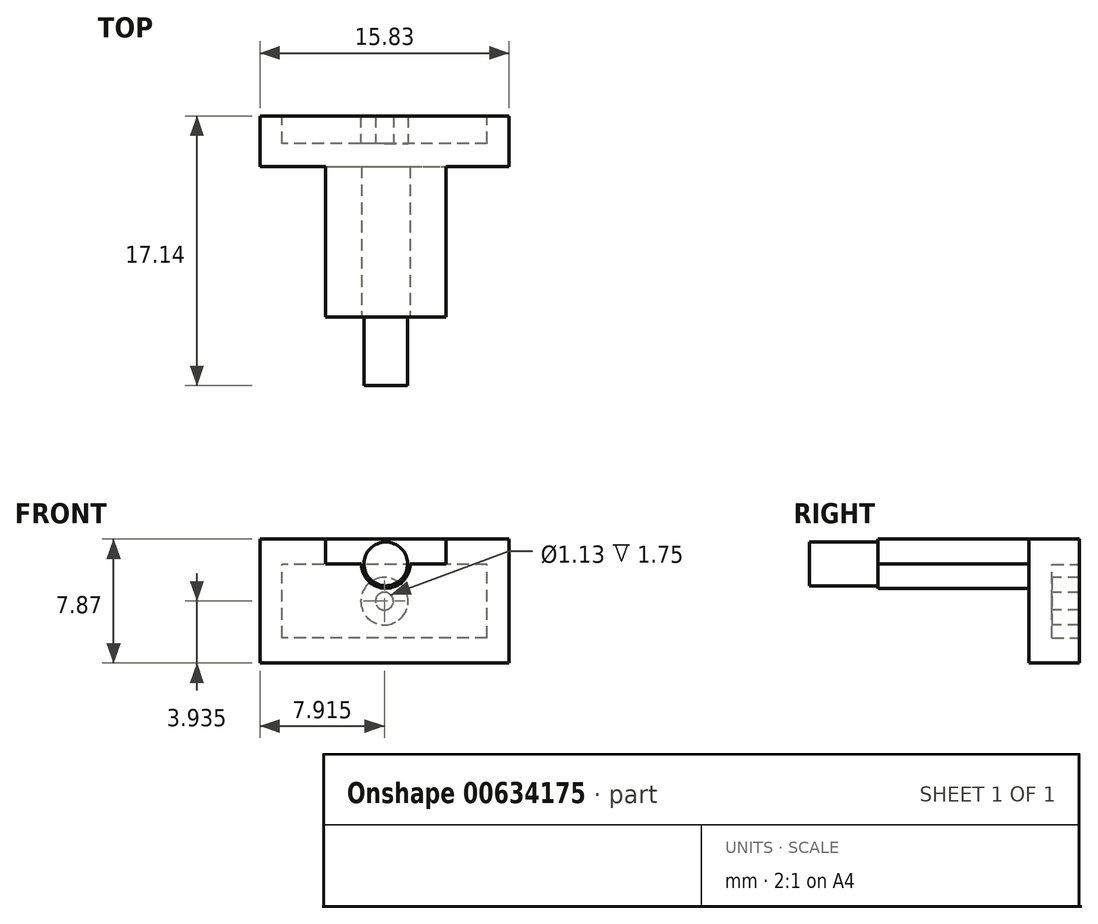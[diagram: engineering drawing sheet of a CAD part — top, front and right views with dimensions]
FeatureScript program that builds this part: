
annotation { "Feature Type Name" : "Feature", "Feature Type Description" : "" }
export const myFeature = defineFeature(function(context is Context, id is Id, definition is map)
    precondition{}
    {
        {
            var Q0;
            Q0=qCreatedBy(makeId("Front.planeOp"),FACE);
            var sketch = newSketch(context, id + "F0", { "sketchPlane" : qUnion([Q0])});
            skLineSegment(sketch, "E0.bottom", {"start": v(0, 0) * mm, "end": v(15.83, 0) * mm});
            skLineSegment(sketch, "E0.top", {"start": v(0, 7.87) * mm, "end": v(15.83, 7.87) * mm});
            skLineSegment(sketch, "E0.left", {"start": v(0, 0) * mm, "end": v(0, 7.87) * mm});
            skLineSegment(sketch, "E0.right", {"start": v(15.83, 0) * mm, "end": v(15.83, 7.87) * mm});
            skSolve(sketch);
        }
        {
            var Q0;
            Q0=qSketchRegion(id+"F0",true);
            extrude(context, id + "F1", {"entities" : qUnion([Q0]), "depth" : 3.2 * mm});
        }
        {
            var Q0;
            Q0=makeQuery(id+"F1.opExtrude","CAP_FACE",FACE,{"disambiguationData":[OSD([sQuery(id+"F0.wireOp",EDGE,"E0.bottom"),sQuery(id+"F0.wireOp",EDGE,"E0.top"),sQuery(id+"F0.wireOp",EDGE,"E0.left"),sQuery(id+"F0.wireOp",EDGE,"E0.right")])],"isStart":true});
            var sketch = newSketch(context, id + "F2", { "sketchPlane" : qUnion([Q0])});
            skLineSegment(sketch, "E1.bottom", {"start": v(-14.43, 1.6) * mm, "end": v(-1.4, 1.6) * mm});
            skLineSegment(sketch, "E1.top", {"start": v(-14.43, 6.27) * mm, "end": v(-1.4, 6.27) * mm});
            skLineSegment(sketch, "E1.left", {"start": v(-14.43, 1.6) * mm, "end": v(-14.43, 6.27) * mm});
            skLineSegment(sketch, "E1.right", {"start": v(-1.4, 1.6) * mm, "end": v(-1.4, 6.27) * mm});
            skSolve(sketch);
        }
        {
            var Q0;
            Q0=qSketchRegion(id+"F2",true);
            extrude(context, id + "F3", {"entities" : qUnion([Q0]), "operationType" : NewBodyOperationType.REMOVE, "oppositeDirection" : true, "depth" : 1.75 * mm});
        }
        {
            var Q0;
            Q0=makeQuery(id+"F3.boolean.opBoolean","COPY",FACE,{"derivedFrom":makeQuery(id+"F3.opExtrude","CAP_FACE",FACE,{"disambiguationData":[OSD([sQuery(id+"F2.wireOp",EDGE,"E1.bottom"),sQuery(id+"F2.wireOp",EDGE,"E1.top"),sQuery(id+"F2.wireOp",EDGE,"E1.left"),sQuery(id+"F2.wireOp",EDGE,"E1.right")])],"isStart":false})});
            var sketch = newSketch(context, id + "F4", { "sketchPlane" : qUnion([Q0])});
            skCircle(sketch, "E2", {"center": v(-7.92, 3.93) * mm, "radius": 1.5 * mm});
            skPoint(sketch, "E2.centerSnap0", {"position": v(-1.4, 3.93) * mm});
            skPoint(sketch, "E2.centerSnap1", {"position": v(-7.92, 6.27) * mm});
            skCircle(sketch, "E3", {"center": v(-7.92, 3.93) * mm, "radius": 0.56 * mm});
            skSolve(sketch);
        }
        {
            var Q0;
            Q0=qSketchRegion(id+"F4",true);
            var Q1;
            Q1=makeQuery(id+"F1.opExtrude","CAP_FACE",FACE,{"disambiguationData":[OSD([sQuery(id+"F0.wireOp",EDGE,"E0.bottom"),sQuery(id+"F0.wireOp",EDGE,"E0.top"),sQuery(id+"F0.wireOp",EDGE,"E0.left"),sQuery(id+"F0.wireOp",EDGE,"E0.right")])],"isStart":true});
            extrude(context, id + "F5", {"entities" : qUnion([Q0]), "operationType" : NewBodyOperationType.ADD, "endBound" : BoundingType.UP_TO_SURFACE, "endBoundEntityFace" : qUnion([Q1]), "depth" : 2 * mm});
        }
        {
            var Q0;
            Q0=makeQuery(id+"F1.opExtrude","CAP_FACE",FACE,{"disambiguationData":[OSD([sQuery(id+"F0.wireOp",EDGE,"E0.bottom"),sQuery(id+"F0.wireOp",EDGE,"E0.top"),sQuery(id+"F0.wireOp",EDGE,"E0.left"),sQuery(id+"F0.wireOp",EDGE,"E0.right")])],"isStart":false});
            var sketch = newSketch(context, id + "F6", { "sketchPlane" : qUnion([Q0])});
            skLineSegment(sketch, "E4.bottom", {"start": v(4.17, 7.87) * mm, "end": v(11.83, 7.87) * mm});
            skLineSegment(sketch, "E4.top", {"start": v(4.17, 6.3) * mm, "end": v(11.83, 6.3) * mm});
            skLineSegment(sketch, "E4.left", {"start": v(4.17, 7.87) * mm, "end": v(4.17, 6.3) * mm});
            skLineSegment(sketch, "E4.right", {"start": v(11.83, 7.87) * mm, "end": v(11.83, 6.3) * mm});
            skSolve(sketch);
        }
        {
            var Q0;
            Q0=qSketchRegion(id+"F6",true);
            extrude(context, id + "F7", {"entities" : qUnion([Q0]), "operationType" : NewBodyOperationType.ADD, "depth" : 9.58 * mm});
        }
        {
            var Q0;
            Q0=makeQuery(id+"F7.opExtrude","CAP_FACE",FACE,{"disambiguationData":[OSD([sQuery(id+"F6.wireOp",EDGE,"E4.bottom"),sQuery(id+"F6.wireOp",EDGE,"E4.top"),sQuery(id+"F6.wireOp",EDGE,"E4.left"),sQuery(id+"F6.wireOp",EDGE,"E4.right")])],"isStart":false});
            var sketch = newSketch(context, id + "F8", { "sketchPlane" : qUnion([Q0])});
            skCircle(sketch, "E5", {"center": v(8, 6.3) * mm, "radius": 1.55 * mm});
            skSolve(sketch);
        }
        {
            var Q0;
            Q0=qSketchRegion(id+"F8",true);
            var Q1;
            Q1=makeQuery(id+"F1.opExtrude","CAP_FACE",FACE,{"disambiguationData":[OSD([sQuery(id+"F0.wireOp",EDGE,"E0.bottom"),sQuery(id+"F0.wireOp",EDGE,"E0.top"),sQuery(id+"F0.wireOp",EDGE,"E0.left"),sQuery(id+"F0.wireOp",EDGE,"E0.right")])],"isStart":false});
            extrude(context, id + "F9", {"entities" : qUnion([Q0]), "operationType" : NewBodyOperationType.ADD, "endBound" : BoundingType.UP_TO_SURFACE, "oppositeDirection" : true, "endBoundEntityFace" : qUnion([Q1]), "depth" : 25 * mm});
        }
        {
            var Q0;
            Q0=makeQuery(id+"F9.boolean.opBoolean","MERGE",FACE,{"derivedFrom":[makeQuery(id+"F7.opExtrude","CAP_FACE",FACE,{"disambiguationData":[OSD([sQuery(id+"F6.wireOp",EDGE,"E4.bottom"),sQuery(id+"F6.wireOp",EDGE,"E4.top"),sQuery(id+"F6.wireOp",EDGE,"E4.left"),sQuery(id+"F6.wireOp",EDGE,"E4.right")])],"isStart":false}),makeQuery(id+"F9.opExtrude","CAP_FACE",FACE,{"disambiguationData":[OSD([sQuery(id+"F8.wireOp",EDGE,"E5")])],"isStart":true})]});
            var sketch = newSketch(context, id + "F10", { "sketchPlane" : qUnion([Q0])});
            skCircle(sketch, "E6", {"center": v(8, 6.3) * mm, "radius": 1.39 * mm});
            skSolve(sketch);
        }
        {
            var Q0;
            Q0=qSketchRegion(id+"F10",true);
            extrude(context, id + "F11", {"entities" : qUnion([Q0]), "operationType" : NewBodyOperationType.ADD, "depth" : 4.35 * mm});
        }
    });
